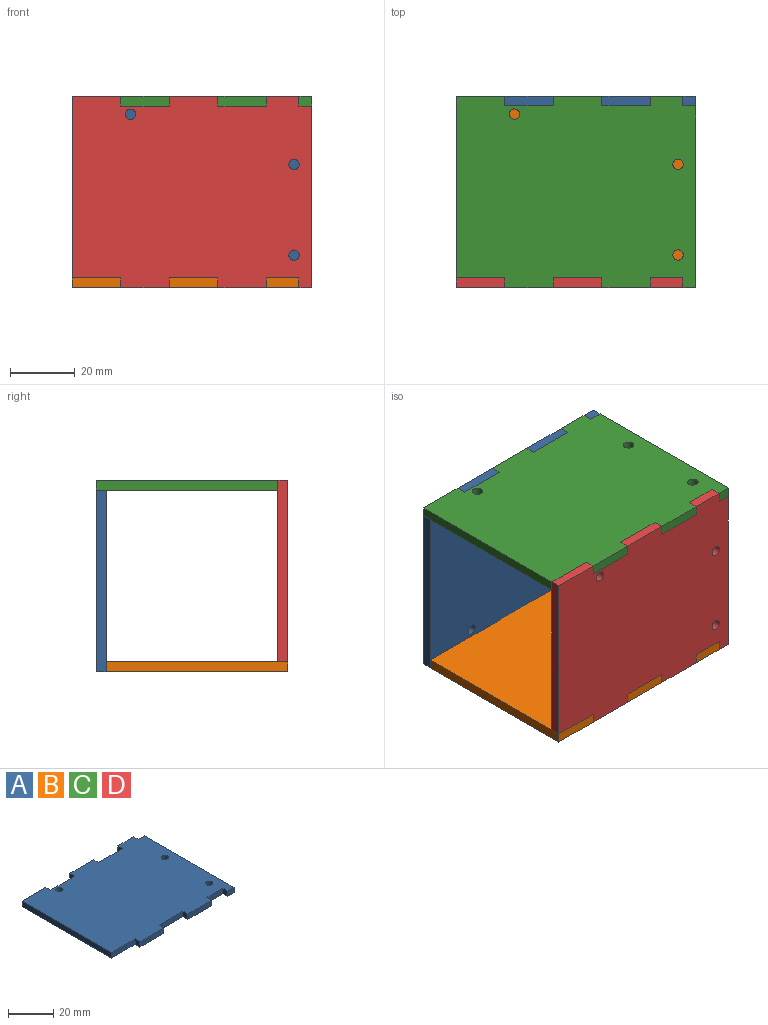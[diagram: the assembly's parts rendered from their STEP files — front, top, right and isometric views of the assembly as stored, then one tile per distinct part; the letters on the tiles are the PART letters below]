
ASSEMBLY  parts=4 mates=3
PART A: 29 faces, bbox 74x59x3 mm
  f0: plane 56x3mm, normal (-1,0,0), area 168mm2, adj f1,f25,f27,f28
  f1: plane 15x3mm, normal (0,-1,0), area 45mm2, adj f0,f2,f27,f28
  f2: plane 3x3mm, normal (-1,0,0), area 9mm2, adj f1,f3,f27,f28
  f3: plane 15x3mm, normal (0,-1,0), area 45mm2, adj f2,f4,f27,f28
  f4: plane 3x3mm, normal (1,0,0), area 9mm2, adj f3,f5,f27,f28
  f5: plane 15x3mm, normal (0,-1,0), area 45mm2, adj f4,f6,f27,f28
  f6: plane 3x3mm, normal (-1,0,0), area 9mm2, adj f5,f7,f27,f28
  f7: plane 15x3mm, normal (0,-1,0), area 45mm2, adj f6,f8,f27,f28
  f8: plane 3x3mm, normal (1,0,0), area 9mm2, adj f7,f9,f27,f28
  f9: plane 10x3mm, normal (0,-1,0), area 30mm2, adj f8,f10,f27,f28
  f10: plane 3x3mm, normal (-1,0,0), area 9mm2, adj f9,f11,f27,f28
  f11: plane 4x3mm, normal (0,-1,0), area 12mm2, adj f10,f12,f27,f28
  f12: plane 56x3mm, normal (1,0,0), area 168mm2, adj f11,f13,f27,f28
  f13: plane 4x3mm, normal (0,1,0), area 12mm2, adj f12,f14,f27,f28
  f14: plane 3x3mm, normal (1,0,0), area 9mm2, adj f13,f15,f27,f28
  f15: plane 10x3mm, normal (0,1,0), area 30mm2, adj f14,f16,f27,f28
  f16: plane 3x3mm, normal (-1,0,0), area 9mm2, adj f15,f17,f27,f28
  f17: plane 15x3mm, normal (0,1,0), area 45mm2, adj f16,f18,f27,f28
  f18: plane 3x3mm, normal (1,0,0), area 9mm2, adj f17,f19,f27,f28
  f19: plane 15x3mm, normal (0,1,0), area 45mm2, adj f18,f20,f27,f28
  f20: plane 3x3mm, normal (-1,0,0), area 9mm2, adj f19,f21,f27,f28
  f21: plane 15x3mm, normal (0,1,0), area 45mm2, adj f20,f22,f27,f28
  f22: plane 3x3mm, normal (1,0,0), area 9mm2, adj f21,f25,f27,f28
  f23: cylinder r=1.6mm len=3.2mm, axis (0,0,-1), area 30.2mm2, adj f27,f28
  f24: cylinder r=1.6mm len=3.2mm, axis (0,0,-1), area 30.2mm2, adj f27,f28
  f25: plane 15x3mm, normal (0,1,0), area 45mm2, adj f0,f22,f27,f28
  f26: cylinder r=1.6mm len=3.2mm, axis (0,0,-1), area 30.2mm2, adj f27,f28
  f27: plane 74x59mm, normal (0,0,1), area 4119.9mm2, adj f0,f1,f2,f3,f4,f5,f6,f7
  f28: plane 74x59mm, normal (0,0,-1), area 4119.9mm2, adj f0,f1,f2,f3,f4,f5,f6,f7
PART B: same geometry as A
PART C: same geometry as A
PART D: same geometry as A
PLACE A rot(axis=(-1,0,0),90deg) t=(-79.67,13.34,49.07)mm
PLACE B rot(axis=(1,0,0),180deg) t=(-79.67,-13.16,22.57)mm
PLACE C t=(-79.67,-13.16,75.57)mm
PLACE D rot(axis=(1,0,0),90deg) t=(-79.67,-39.66,49.07)mm
MATE fastened B.f14 <-> D.f10  axis (1,0,0) through (-46.67,-41.16,21.07)mm
MATE fastened A.f10 <-> C.f14  axis (-1,0,0) through (-46.67,14.84,77.07)mm
MATE fastened D.f14 <-> C.f10  axis (1,0,0) through (-46.67,-41.16,77.07)mm
